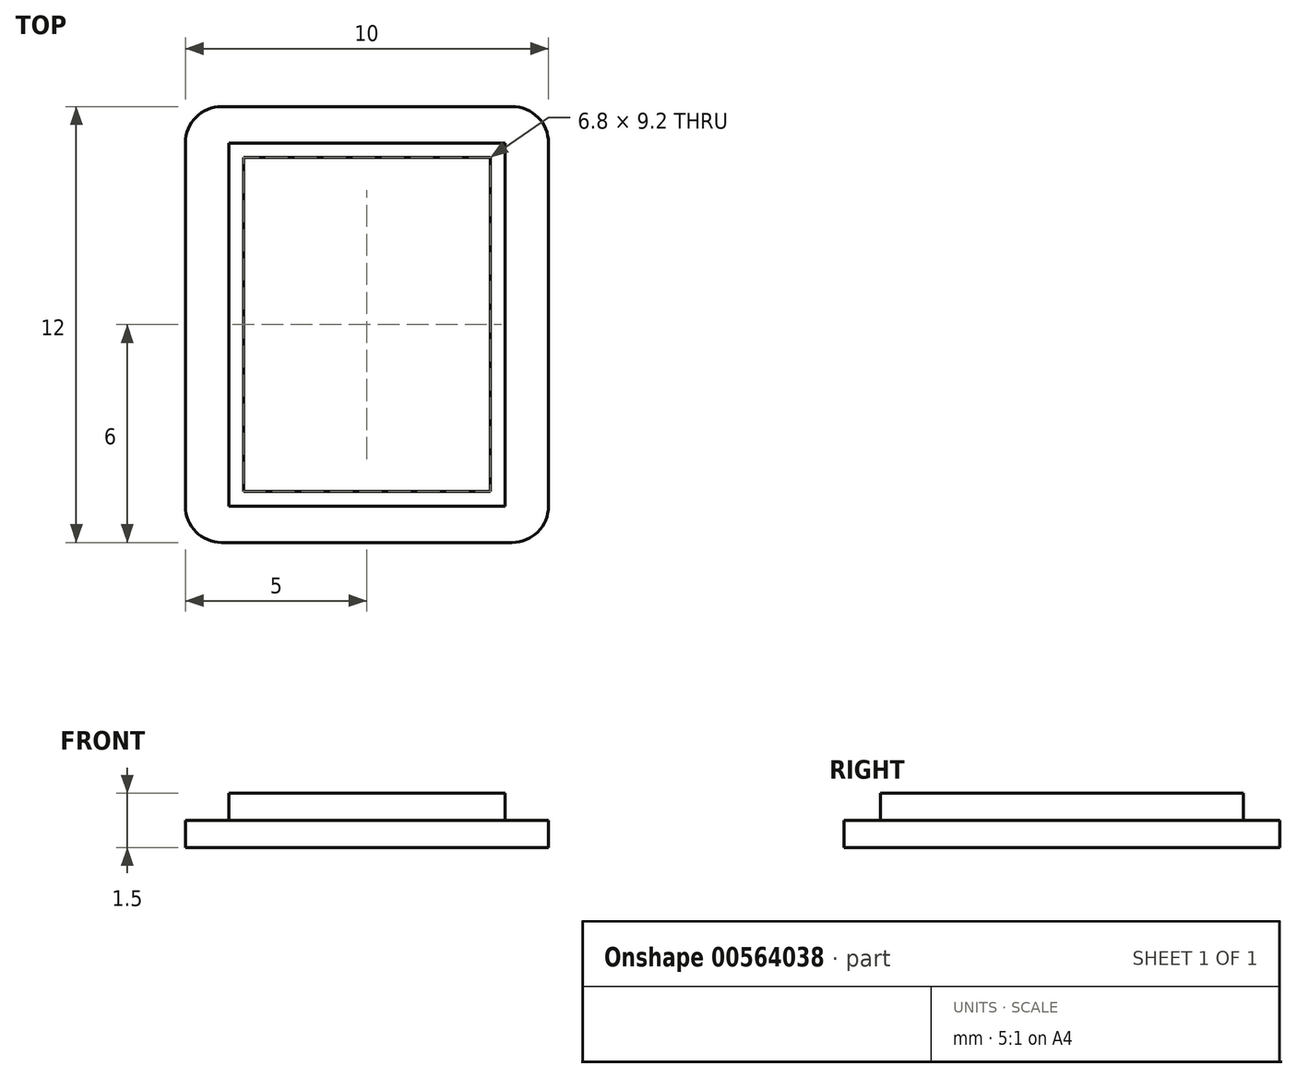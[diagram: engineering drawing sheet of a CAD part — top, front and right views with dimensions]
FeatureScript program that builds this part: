
annotation { "Feature Type Name" : "Feature", "Feature Type Description" : "" }
export const myFeature = defineFeature(function(context is Context, id is Id, definition is map)
    precondition{}
    {
        {
            var Q0;
            Q0=qCreatedBy(makeId("Top.planeOp"),FACE);
            var sketch = newSketch(context, id + "F0", { "sketchPlane" : qUnion([Q0])});
            skLineSegment(sketch, "E0.bottom", {"start": v(5, -6) * mm, "end": v(-5, -6) * mm});
            skLineSegment(sketch, "E0.top", {"start": v(5, 6) * mm, "end": v(-5, 6) * mm});
            skLineSegment(sketch, "E0.left", {"start": v(5, -6) * mm, "end": v(5, 6) * mm});
            skLineSegment(sketch, "E0.right", {"start": v(-5, -6) * mm, "end": v(-5, 6) * mm});
            skPoint(sketch, "E0.middle", {"position": v(0, 0) * mm});
            skLineSegment(sketch, "E1.bottom", {"start": v(3.8, -5) * mm, "end": v(-3.8, -5) * mm});
            skLineSegment(sketch, "E1.top", {"start": v(3.8, 5) * mm, "end": v(-3.8, 5) * mm});
            skLineSegment(sketch, "E1.left", {"start": v(3.8, -5) * mm, "end": v(3.8, 5) * mm});
            skLineSegment(sketch, "E1.right", {"start": v(-3.8, -5) * mm, "end": v(-3.8, 5) * mm});
            skLineSegment(sketch, "E2.bottom", {"start": v(3.4, -4.6) * mm, "end": v(-3.4, -4.6) * mm});
            skLineSegment(sketch, "E2.top", {"start": v(3.4, 4.6) * mm, "end": v(-3.4, 4.6) * mm});
            skLineSegment(sketch, "E2.left", {"start": v(3.4, -4.6) * mm, "end": v(3.4, 4.6) * mm});
            skLineSegment(sketch, "E2.right", {"start": v(-3.4, -4.6) * mm, "end": v(-3.4, 4.6) * mm});
            skSolve(sketch);
        }
        {
            var Q0;
            Q0=makeQuery(id+"F0.imprint","IMPRINT",FACE,{"disambiguationData":[TD([[makeQuery(id+"F0.imprint","IMPRINT",EDGE,{"derivedFrom":sQuery(id+"F0.wireOp",EDGE,"E0.bottom")}),-1.0]])]});
            extrude(context, id + "F1", {"entities" : qUnion([Q0]), "depth" : 0.75 * mm, "offsetDistance" : 25 * mm});
        }
        {
            var Q0;
            Q0=makeQuery(id+"F0.imprint","IMPRINT",FACE,{"disambiguationData":[TD([[makeQuery(id+"F0.imprint","IMPRINT",EDGE,{"derivedFrom":sQuery(id+"F0.wireOp",EDGE,"E1.bottom")}),-1.0]])]});
            extrude(context, id + "F2", {"entities" : qUnion([Q0]), "operationType" : NewBodyOperationType.ADD, "depth" : 1.5 * mm, "offsetDistance" : 25 * mm});
        }
        {
            var Q0;
            Q0=makeQuery(id+"F1.opExtrude","SWEPT_EDGE",EDGE,{"disambiguationData":[OSD([sQuery(id+"F0.wireOp",EDGE,"E0.top"),sQuery(id+"F0.wireOp",EDGE,"E0.left")])]});
            var Q1;
            Q1=makeQuery(id+"F1.opExtrude","SWEPT_EDGE",EDGE,{"disambiguationData":[OSD([sQuery(id+"F0.wireOp",EDGE,"E0.top"),sQuery(id+"F0.wireOp",EDGE,"E0.right")])]});
            var Q2;
            Q2=makeQuery(id+"F1.opExtrude","SWEPT_EDGE",EDGE,{"disambiguationData":[OSD([sQuery(id+"F0.wireOp",EDGE,"E0.bottom"),sQuery(id+"F0.wireOp",EDGE,"E0.right")])]});
            var Q3;
            Q3=makeQuery(id+"F1.opExtrude","SWEPT_EDGE",EDGE,{"disambiguationData":[OSD([sQuery(id+"F0.wireOp",EDGE,"E0.bottom"),sQuery(id+"F0.wireOp",EDGE,"E0.left")])]});
            fillet(context, id + "F3", {"entities" : qUnion([Q0, Q1, Q2, Q3]), "radius" : 1 * mm, "tangentPropagation" : true, "allowEdgeOverflow" : false});
        }
    });
